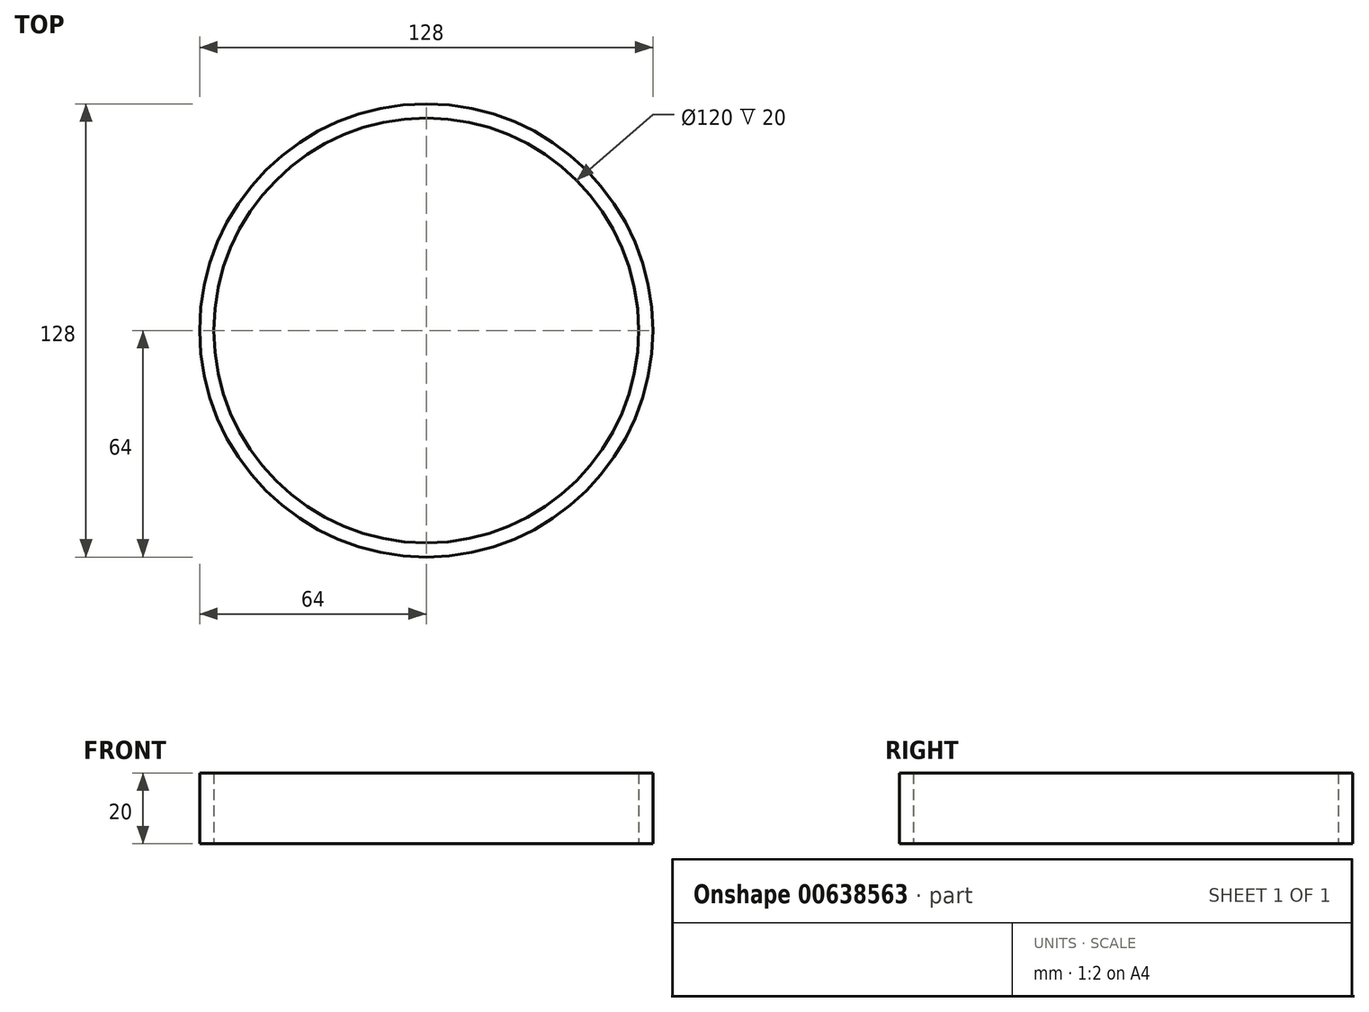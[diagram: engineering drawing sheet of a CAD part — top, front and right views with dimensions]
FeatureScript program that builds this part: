
annotation { "Feature Type Name" : "Feature", "Feature Type Description" : "" }
export const myFeature = defineFeature(function(context is Context, id is Id, definition is map)
    precondition{}
    {
        {
            var Q0;
            Q0=qCreatedBy(makeId("Top.planeOp"),FACE);
            var sketch = newSketch(context, id + "F0", { "sketchPlane" : qUnion([Q0])});
            skCircle(sketch, "E0", {"center": v(0, 0) * mm, "radius": 64 * mm});
            skCircle(sketch, "E1.0", {"center": v(0, 0) * mm, "radius": 60 * mm});
            skSolve(sketch);
        }
        {
            var Q0;
            Q0 = qSketchRegion(id + "F0", true);
            extrude(context, id + "F1", {"entities" : qUnion([Q0]), "depth" : 20 * mm, "offsetDistance" : 25 * mm});
        }
    });
